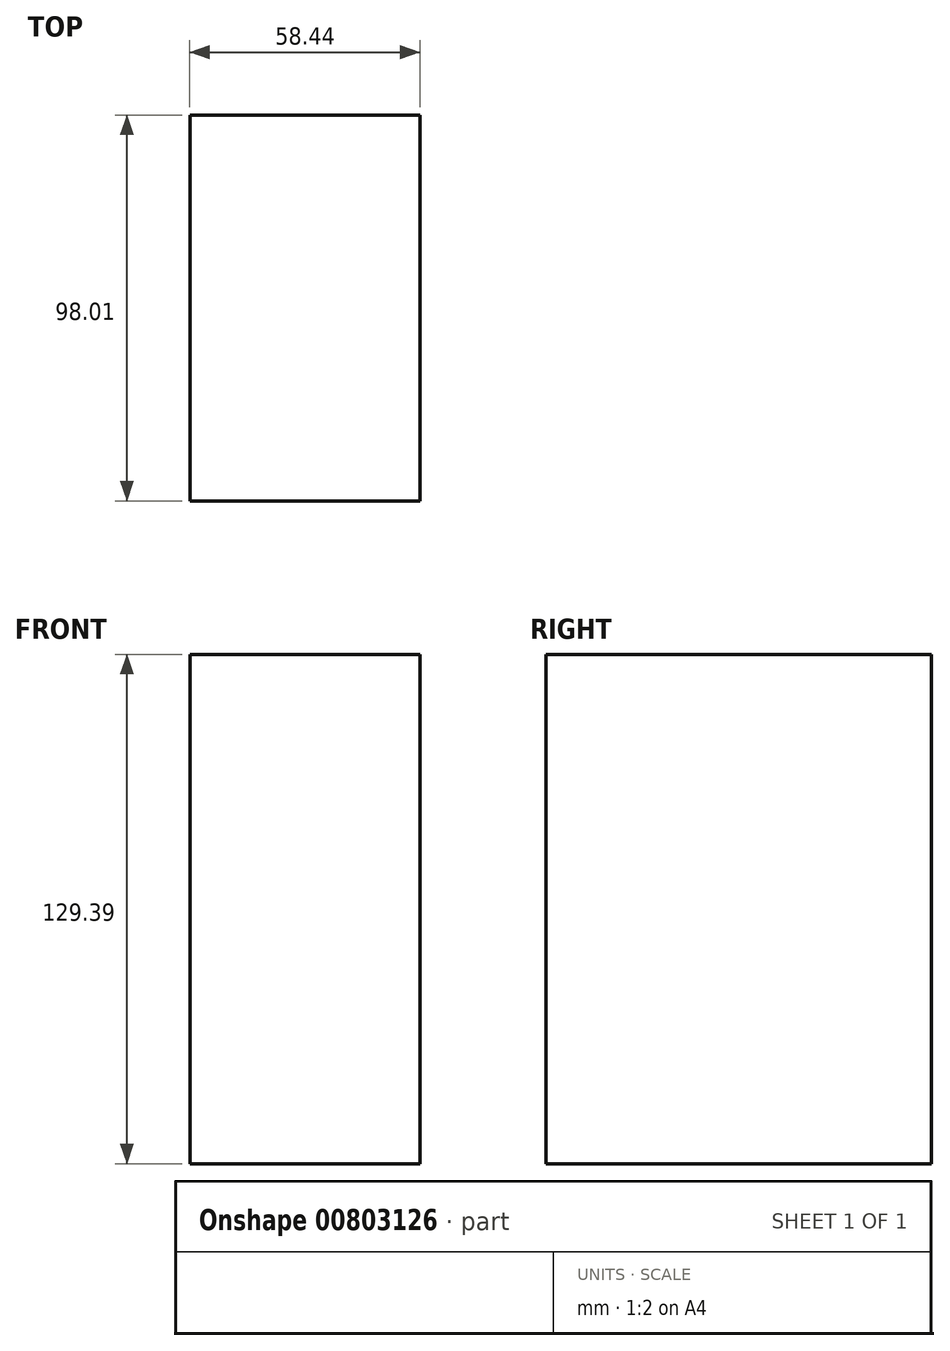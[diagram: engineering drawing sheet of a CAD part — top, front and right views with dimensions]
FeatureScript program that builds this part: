
annotation { "Feature Type Name" : "Feature", "Feature Type Description" : "" }
export const myFeature = defineFeature(function(context is Context, id is Id, definition is map)
    precondition{}
    {
        {
            var Q0;
            Q0=qCreatedBy(makeId("Top.planeOp"),FACE);
            var sketch = newSketch(context, id + "F0", { "sketchPlane" : qUnion([Q0])});
            skLineSegment(sketch, "E0.bottom", {"start": v(39.04, 42.38) * mm, "end": v(97.48, 42.38) * mm});
            skLineSegment(sketch, "E0.top", {"start": v(39.04, -55.63) * mm, "end": v(97.48, -55.63) * mm});
            skLineSegment(sketch, "E0.left", {"start": v(39.04, 42.38) * mm, "end": v(39.04, -55.63) * mm});
            skLineSegment(sketch, "E0.right", {"start": v(97.48, 42.38) * mm, "end": v(97.48, -55.63) * mm});
            skSolve(sketch);
        }
        {
            var Q0;
            Q0=makeQuery(id+"F0.imprint","IMPRINT",FACE,{"disambiguationData":[TD([[makeQuery(id+"F0.imprint","IMPRINT",EDGE,{"derivedFrom":sQuery(id+"F0.wireOp",EDGE,"E0.bottom")}),-1.0]])]});
            extrude(context, id + "F1", {"entities" : qUnion([Q0]), "depth" : 129.4 * mm, "offsetDistance" : 25.4 * mm});
        }
    });
